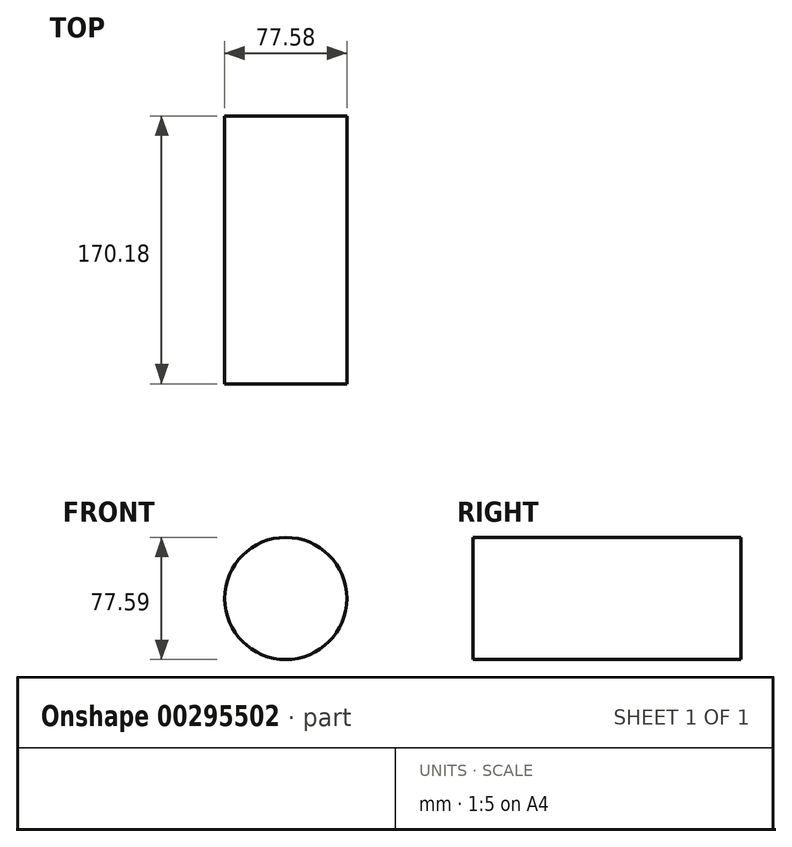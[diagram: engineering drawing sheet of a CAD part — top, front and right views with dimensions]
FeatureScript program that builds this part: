
annotation { "Feature Type Name" : "Feature", "Feature Type Description" : "" }
export const myFeature = defineFeature(function(context is Context, id is Id, definition is map)
    precondition{}
    {
        {
            var Q0;
            Q0=qCreatedBy(makeId("Front.planeOp"),FACE);
            var sketch = newSketch(context, id + "F0", { "sketchPlane" : qUnion([Q0])});
            skCircle(sketch, "E0", {"center": v(-8.13, -16.58) * mm, "radius": 38.8 * mm});
            skSolve(sketch);
        }
        {
            var Q0;
            Q0=sQuery(id+"F0.wireOp",EDGE,"E0");
            extrude(context, id + "F1", {"bodyType" : ToolBodyType.SURFACE, "surfaceEntities" : qUnion([Q0]), "depth" : 170.18 * mm});
        }
    });
